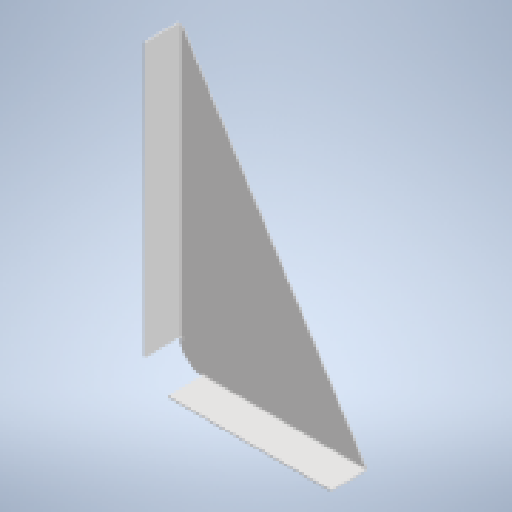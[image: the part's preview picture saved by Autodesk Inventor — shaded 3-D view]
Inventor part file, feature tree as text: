
AUTODESK INVENTOR PART (.ipt)
format: ipt  version: 2025.2 (Build 292293000, 293)  size: 209,920 bytes
history: native  units: mm
features: sheet_metal_op x4, other x3, sketch x2
ambient origin geometry x8: Origin, YZ Plane, XZ Plane, XY Plane, X Axis, Y Axis, Z Axis, Center Point
bodies: Solid1 (feature_tree)
feature tree (9):
  sheet_metal_op  "Face1"
  sheet_metal_op  "Flange1"
  sketch  "Sketch1"  dims[d0=76.2mm]
  other  "Plate1"
  sketch  "Sketch2"  dims[d1=120.65mm d2=1.5875mm d3=1.5875mm d4=0.79375mm d5=3.175mm d6=1.5875mm d7=20.0mm d8=90.0deg d9=1.5875mm d10=6.35mm d11=1.5875mm d12=1.5875mm d13=9.525mm d14=6.35mm d15=10.0mm]
  other  "Plate2"
  sheet_metal_op  "Bend1"
  sheet_metal_op  "Corner1"
  other  "Definition1"
